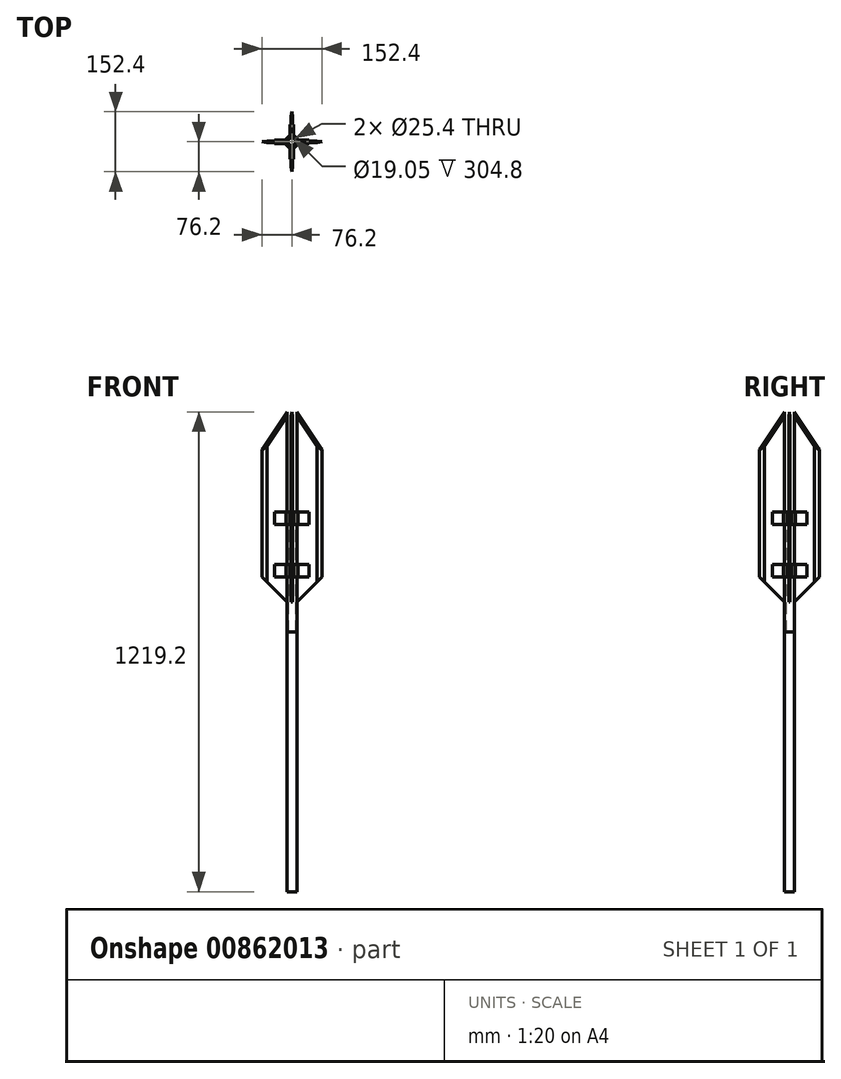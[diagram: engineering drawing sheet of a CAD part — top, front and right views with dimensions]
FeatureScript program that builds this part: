
annotation { "Feature Type Name" : "Feature", "Feature Type Description" : "" }
export const myFeature = defineFeature(function(context is Context, id is Id, definition is map)
    precondition{}
    {
        {
            var Q0;
            Q0=qCreatedBy(makeId("Top.planeOp"),FACE);
            var sketch = newSketch(context, id + "F0", { "sketchPlane" : qUnion([Q0])});
            skCircle(sketch, "E0", {"center": v(0, 0) * mm, "radius": 12.7 * mm});
            skCircle(sketch, "E1", {"center": v(0, 0) * mm, "radius": 9.53 * mm});
            skSolve(sketch);
        }
        {
            var Q0;
            Q0=makeQuery(id+"F0.imprint","IMPRINT",FACE,{"disambiguationData":[TD([[makeQuery(id+"F0.imprint","IMPRINT",EDGE,{"derivedFrom":sQuery(id+"F0.wireOp",EDGE,"E0")}),1.0]])]});
            extrude(context, id + "F1", {"entities" : qUnion([Q0]), "depth" : 914.4 * mm, "offsetDistance" : 25.4 * mm, "hasSecondDirection" : true, "secondDirectionOppositeDirection" : false, "secondDirectionDepth" : 254 * mm});
        }
        {
            var Q0;
            Q0=makeQuery(id+"F0.imprint","IMPRINT",FACE,{"disambiguationData":[TD([[makeQuery(id+"F0.imprint","IMPRINT",EDGE,{"derivedFrom":sQuery(id+"F0.wireOp",EDGE,"E1")}),1.0]])]});
            extrude(context, id + "F2", {"entities" : qUnion([Q0]), "operationType" : NewBodyOperationType.ADD, "depth" : 1219.2 * mm, "offsetDistance" : 25.4 * mm, "hasSecondDirection" : true, "secondDirectionOppositeDirection" : false, "secondDirectionDepth" : 254 * mm});
        }
        {
            var Q0;
            Q0=makeQuery(id+"F0.imprint","IMPRINT",FACE,{"disambiguationData":[TD([[makeQuery(id+"F0.imprint","IMPRINT",EDGE,{"derivedFrom":sQuery(id+"F0.wireOp",EDGE,"E0")}),1.0]])]});
            extrude(context, id + "F3", {"entities" : qUnion([Q0]), "depth" : 1219.2 * mm, "offsetDistance" : 25.4 * mm, "hasSecondDirection" : true, "secondDirectionOppositeDirection" : false, "secondDirectionDepth" : 914.4 * mm});
        }
        {
            var Q0;
            Q0=qCreatedBy(makeId("Front.planeOp"),FACE);
            var sketch = newSketch(context, id + "F4", { "sketchPlane" : qUnion([Q0])});
            skLineSegment(sketch, "E2.left", {"start": v(12.7, 1473.2) * mm, "end": v(12.7, 990.6) * mm});
            skLineSegment(sketch, "E2.right", {"start": v(76.2, 1377.95) * mm, "end": v(76.2, 1054.1) * mm});
            skLineSegment(sketch, "E3.left", {"start": v(-12.7, 1473.2) * mm, "end": v(-12.7, 990.6) * mm});
            skLineSegment(sketch, "E3.right", {"start": v(-76.2, 1377.95) * mm, "end": v(-76.2, 1054.1) * mm});
            skLineSegment(sketch, "E4", {"start": v(-76.2, 1054.1) * mm, "end": v(-12.7, 990.6) * mm});
            skLineSegment(sketch, "E5", {"start": v(12.7, 990.6) * mm, "end": v(76.2, 1054.1) * mm});
            skPoint(sketch, "E6.orphan", {"position": v(-76.2, 990.6) * mm});
            skLineSegment(sketch, "E7", {"start": v(-12.7, 1473.2) * mm, "end": v(-76.2, 1377.95) * mm});
            skLineSegment(sketch, "E8", {"start": v(12.7, 1473.2) * mm, "end": v(76.2, 1377.95) * mm});
            skPoint(sketch, "E9.orphan", {"position": v(-76.2, 1473.2) * mm});
            skSolve(sketch);
        }
        {
            var Q0;
            Q0=makeQuery(id+"F4.imprint","IMPRINT",FACE,{"disambiguationData":[TD([[makeQuery(id+"F4.imprint","IMPRINT",EDGE,{"derivedFrom":sQuery(id+"F4.wireOp",EDGE,"E3.left")}),-1.0]])]});
            var Q1;
            Q1=makeQuery(id+"F4.imprint","IMPRINT",FACE,{"disambiguationData":[TD([[makeQuery(id+"F4.imprint","IMPRINT",EDGE,{"derivedFrom":sQuery(id+"F4.wireOp",EDGE,"E2.left")}),1.0]])]});
            extrude(context, id + "F5", {"entities" : qUnion([Q0, Q1]), "operationType" : NewBodyOperationType.ADD, "depth" : 1.59 * mm, "offsetDistance" : 25.4 * mm, "hasSecondDirection" : true, "secondDirectionOppositeDirection" : true, "secondDirectionDepth" : 1.59 * mm});
        }
        {
            var Q0;
            Q0=qCreatedBy(makeId("Right.planeOp"),FACE);
            var sketch = newSketch(context, id + "F6", { "sketchPlane" : qUnion([Q0])});
            skLineSegment(sketch, "E10.left", {"start": v(12.7, 990.6) * mm, "end": v(12.7, 1473.2) * mm});
            skLineSegment(sketch, "E10.right", {"start": v(76.2, 1054.1) * mm, "end": v(76.2, 1377.95) * mm});
            skLineSegment(sketch, "E11.left", {"start": v(-12.7, 990.6) * mm, "end": v(-12.7, 1473.2) * mm});
            skLineSegment(sketch, "E11.right", {"start": v(-76.2, 1054.1) * mm, "end": v(-76.2, 1377.95) * mm});
            skLineSegment(sketch, "E12", {"start": v(12.7, 990.6) * mm, "end": v(76.2, 1054.1) * mm});
            skLineSegment(sketch, "E13", {"start": v(-12.7, 990.6) * mm, "end": v(-76.2, 1054.1) * mm});
            skLineSegment(sketch, "E14", {"start": v(12.7, 1473.2) * mm, "end": v(76.2, 1377.95) * mm});
            skLineSegment(sketch, "E15", {"start": v(-12.7, 1473.2) * mm, "end": v(-76.2, 1377.95) * mm});
            skPoint(sketch, "E10.bottom.end.orphan", {"position": v(76.2, 990.6) * mm});
            skPoint(sketch, "E16.orphan", {"position": v(76.2, 1473.2) * mm});
            skPoint(sketch, "E17.orphan", {"position": v(-76.2, 1473.2) * mm});
            skSolve(sketch);
        }
        {
            var Q0;
            Q0=makeQuery(id+"F6.imprint","IMPRINT",FACE,{"disambiguationData":[TD([[makeQuery(id+"F6.imprint","IMPRINT",EDGE,{"derivedFrom":sQuery(id+"F6.wireOp",EDGE,"E11.left")}),1.0]])]});
            var Q1;
            Q1=makeQuery(id+"F6.imprint","IMPRINT",FACE,{"disambiguationData":[TD([[makeQuery(id+"F6.imprint","IMPRINT",EDGE,{"derivedFrom":sQuery(id+"F6.wireOp",EDGE,"E10.left")}),-1.0]])]});
            extrude(context, id + "F7", {"entities" : qUnion([Q0, Q1]), "operationType" : NewBodyOperationType.ADD, "depth" : 1.59 * mm, "offsetDistance" : 25.4 * mm, "hasSecondDirection" : true, "secondDirectionOppositeDirection" : true, "secondDirectionDepth" : 1.59 * mm});
        }
        {
            var Q0;
            Q0=qCreatedBy(makeId("Top.planeOp"),FACE);
            var sketch = newSketch(context, id + "F8", { "sketchPlane" : qUnion([Q0])});
            skArc(sketch, "E18", {"start": v(15.14, 4.76) * mm, "mid": v(11.23, 11.23) * mm, "end": v(4.76, 15.14) * mm});
            skLineSegment(sketch, "E19.bottom", {"start": v(15.14, 4.76) * mm, "end": v(43.72, 4.76) * mm});
            skLineSegment(sketch, "E19.top", {"start": v(15.14, -4.76) * mm, "end": v(43.72, -4.76) * mm});
            skLineSegment(sketch, "E19.right", {"start": v(43.72, 4.76) * mm, "end": v(43.72, -4.76) * mm});
            skPoint(sketch, "E19.middle", {"position": v(29.43, 0) * mm});
            skLineSegment(sketch, "E20.top", {"start": v(4.76, 43.72) * mm, "end": v(-4.76, 43.72) * mm});
            skLineSegment(sketch, "E20.left", {"start": v(4.76, 15.14) * mm, "end": v(4.76, 43.72) * mm});
            skLineSegment(sketch, "E20.right", {"start": v(-4.76, 15.14) * mm, "end": v(-4.76, 43.72) * mm});
            skPoint(sketch, "E20.middle", {"position": v(0, 29.43) * mm});
            skLineSegment(sketch, "E21.bottom", {"start": v(-15.14, -4.76) * mm, "end": v(-43.72, -4.76) * mm});
            skLineSegment(sketch, "E21.top", {"start": v(-15.14, 4.76) * mm, "end": v(-43.72, 4.76) * mm});
            skLineSegment(sketch, "E21.right", {"start": v(-43.72, -4.76) * mm, "end": v(-43.72, 4.76) * mm});
            skPoint(sketch, "E21.middle", {"position": v(-29.43, 0) * mm});
            skLineSegment(sketch, "E22.top", {"start": v(4.76, -43.72) * mm, "end": v(-4.76, -43.72) * mm});
            skLineSegment(sketch, "E22.left", {"start": v(4.76, -15.14) * mm, "end": v(4.76, -43.72) * mm});
            skLineSegment(sketch, "E22.right", {"start": v(-4.76, -15.14) * mm, "end": v(-4.76, -43.72) * mm});
            skPoint(sketch, "E22.middle", {"position": v(0, -29.43) * mm});
            skArc(sketch, "E23.trimOffspring", {"start": v(-4.76, 15.14) * mm, "mid": v(-11.23, 11.23) * mm, "end": v(-15.14, 4.76) * mm});
            skArc(sketch, "E24.trimOffspring", {"start": v(-15.14, -4.76) * mm, "mid": v(-11.23, -11.23) * mm, "end": v(-4.76, -15.14) * mm});
            skArc(sketch, "E25.trimOffspring", {"start": v(4.76, -15.14) * mm, "mid": v(11.23, -11.23) * mm, "end": v(15.14, -4.76) * mm});
            skCircle(sketch, "E26", {"center": v(0, 0) * mm, "radius": 12.7 * mm});
            skSolve(sketch);
        }
        {
            var Q0;
            Q0=makeQuery(id+"F8.imprint","IMPRINT",FACE,{"disambiguationData":[TD([[makeQuery(id+"F8.imprint","IMPRINT",EDGE,{"derivedFrom":sQuery(id+"F8.wireOp",EDGE,"E18")}),1.0]])]});
            extrude(context, id + "F9", {"entities" : qUnion([Q0]), "depth" : 1085.85 * mm, "offsetDistance" : 25.4 * mm, "hasSecondDirection" : true, "secondDirectionOppositeDirection" : false, "secondDirectionDepth" : 1054.1 * mm});
        }
        {
            var Q0;
            Q0=makeQuery(id+"F8.imprint","IMPRINT",FACE,{"disambiguationData":[TD([[makeQuery(id+"F8.imprint","IMPRINT",EDGE,{"derivedFrom":sQuery(id+"F8.wireOp",EDGE,"E18")}),1.0]])]});
            extrude(context, id + "F10", {"entities" : qUnion([Q0]), "depth" : 1219.2 * mm, "offsetDistance" : 25.4 * mm, "hasSecondDirection" : true, "secondDirectionOppositeDirection" : false, "secondDirectionDepth" : 1187.45 * mm});
        }
        {
            var Q0;
            Q0=makeQuery(id+"F5.opExtrude","CAP_EDGE",EDGE,{"disambiguationData":[OSD([sQuery(id+"F4.wireOp",EDGE,"E2.right")])],"isStart":false});
            var Q1;
            Q1=makeQuery(id+"F7.opExtrude","CAP_EDGE",EDGE,{"disambiguationData":[OSD([sQuery(id+"F6.wireOp",EDGE,"E11.right")])],"isStart":false});
            var Q2;
            Q2=makeQuery(id+"F5.opExtrude","CAP_EDGE",EDGE,{"disambiguationData":[OSD([sQuery(id+"F4.wireOp",EDGE,"E3.right")])],"isStart":true});
            var Q3;
            Q3=makeQuery(id+"F7.opExtrude","CAP_EDGE",EDGE,{"disambiguationData":[OSD([sQuery(id+"F6.wireOp",EDGE,"E10.right")])],"isStart":true});
            chamfer(context, id + "F11", {"entities" : qUnion([Q0, Q1, Q2, Q3]), "chamferType" : ChamferType.TWO_OFFSETS, "width1" : 1.59 * mm, "oppositeDirection" : false, "width2" : 12.7 * mm, "tangentPropagation" : true});
        }
        {
            var Q0;
            Q0=makeQuery(id+"F7.opExtrude","CAP_EDGE",EDGE,{"disambiguationData":[OSD([sQuery(id+"F6.wireOp",EDGE,"E11.right")])],"isStart":true});
            var Q1;
            Q1=makeQuery(id+"F5.opExtrude","CAP_EDGE",EDGE,{"disambiguationData":[OSD([sQuery(id+"F4.wireOp",EDGE,"E3.right")])],"isStart":false});
            var Q2;
            Q2=makeQuery(id+"F7.opExtrude","CAP_EDGE",EDGE,{"disambiguationData":[OSD([sQuery(id+"F6.wireOp",EDGE,"E10.right")])],"isStart":false});
            var Q3;
            Q3=makeQuery(id+"F5.opExtrude","CAP_EDGE",EDGE,{"disambiguationData":[OSD([sQuery(id+"F4.wireOp",EDGE,"E2.right")])],"isStart":true});
            chamfer(context, id + "F12", {"entities" : qUnion([Q0, Q1, Q2, Q3]), "chamferType" : ChamferType.TWO_OFFSETS, "width1" : 12.7 * mm, "oppositeDirection" : false, "width2" : 1.59 * mm, "tangentPropagation" : true});
        }
        {
            var Q0;
            Q0=makeQuery(id+"F5.opExtrude","CAP_EDGE",EDGE,{"disambiguationData":[OSD([sQuery(id+"F4.wireOp",EDGE,"E8")])],"isStart":true});
            var Q1;
            Q1=makeQuery(id+"F7.opExtrude","CAP_EDGE",EDGE,{"disambiguationData":[OSD([sQuery(id+"F6.wireOp",EDGE,"E14")])],"isStart":true});
            var Q2;
            Q2=makeQuery(id+"F5.opExtrude","CAP_EDGE",EDGE,{"disambiguationData":[OSD([sQuery(id+"F4.wireOp",EDGE,"E7")])],"isStart":false});
            var Q3;
            Q3=makeQuery(id+"F7.opExtrude","CAP_EDGE",EDGE,{"disambiguationData":[OSD([sQuery(id+"F6.wireOp",EDGE,"E15")])],"isStart":false});
            chamfer(context, id + "F13", {"entities" : qUnion([Q0, Q1, Q2, Q3]), "chamferType" : ChamferType.TWO_OFFSETS, "width1" : 6.35 * mm, "oppositeDirection" : false, "width2" : 1.59 * mm, "tangentPropagation" : true});
        }
        {
            var Q0;
            Q0=makeQuery(id+"F5.opExtrude","CAP_EDGE",EDGE,{"disambiguationData":[OSD([sQuery(id+"F4.wireOp",EDGE,"E8")])],"isStart":false});
            var Q1;
            Q1=makeQuery(id+"F7.opExtrude","CAP_EDGE",EDGE,{"disambiguationData":[OSD([sQuery(id+"F6.wireOp",EDGE,"E15")])],"isStart":true});
            var Q2;
            Q2=makeQuery(id+"F5.opExtrude","CAP_EDGE",EDGE,{"disambiguationData":[OSD([sQuery(id+"F4.wireOp",EDGE,"E7")])],"isStart":true});
            var Q3;
            Q3=makeQuery(id+"F7.opExtrude","CAP_EDGE",EDGE,{"disambiguationData":[OSD([sQuery(id+"F6.wireOp",EDGE,"E14")])],"isStart":false});
            chamfer(context, id + "F14", {"entities" : qUnion([Q0, Q1, Q2, Q3]), "chamferType" : ChamferType.TWO_OFFSETS, "width1" : 1.59 * mm, "oppositeDirection" : false, "width2" : 6.35 * mm, "tangentPropagation" : true});
        }
    });
